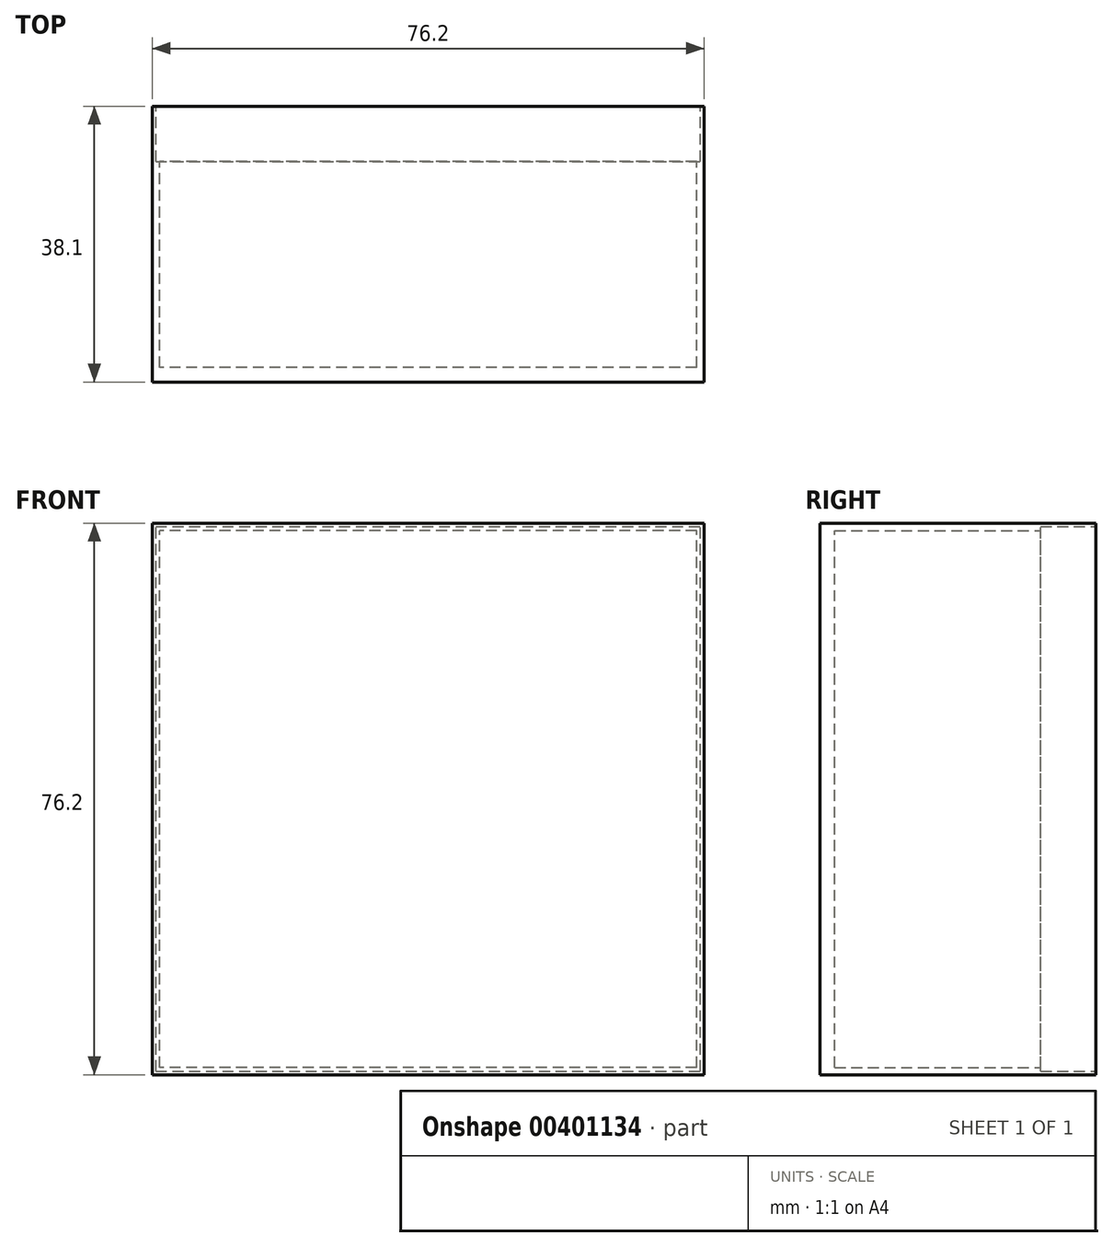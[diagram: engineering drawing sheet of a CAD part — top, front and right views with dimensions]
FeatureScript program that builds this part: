
annotation { "Feature Type Name" : "Feature", "Feature Type Description" : "" }
export const myFeature = defineFeature(function(context is Context, id is Id, definition is map)
    precondition{}
    {
        {
            var Q0;
            Q0=qCreatedBy(makeId("Front.planeOp"),FACE);
            var sketch = newSketch(context, id + "F0", { "sketchPlane" : qUnion([Q0])});
            skLineSegment(sketch, "E0.bottom", {"start": v(38.1, -38.1) * mm, "end": v(-38.1, -38.1) * mm});
            skLineSegment(sketch, "E0.top", {"start": v(38.1, 38.1) * mm, "end": v(-38.1, 38.1) * mm});
            skLineSegment(sketch, "E0.left", {"start": v(38.1, -38.1) * mm, "end": v(38.1, 38.1) * mm});
            skLineSegment(sketch, "E0.right", {"start": v(-38.1, -38.1) * mm, "end": v(-38.1, 38.1) * mm});
            skPoint(sketch, "E0.middle", {"position": v(0, 0) * mm});
            skSolve(sketch);
        }
        {
            var Q0;
            Q0=makeQuery(id+"F0.imprint","IMPRINT",FACE,{"disambiguationData":[TD([[makeQuery(id+"F0.imprint","IMPRINT",EDGE,{"derivedFrom":sQuery(id+"F0.wireOp",EDGE,"E0.bottom")}),-1.0]])]});
            extrude(context, id + "F1", {"entities" : qUnion([Q0]), "depth" : 38.1 * mm});
        }
        {
            var Q0;
            Q0=makeQuery(id+"F1.opExtrude","CAP_FACE",FACE,{"disambiguationData":[OSD([sQuery(id+"F0.wireOp",EDGE,"E0.bottom"),sQuery(id+"F0.wireOp",EDGE,"E0.top"),sQuery(id+"F0.wireOp",EDGE,"E0.left"),sQuery(id+"F0.wireOp",EDGE,"E0.right")])],"isStart":true});
            var sketch = newSketch(context, id + "F2", { "sketchPlane" : qUnion([Q0])});
            skLineSegment(sketch, "E1.bottom", {"start": v(-37.08, -37.08) * mm, "end": v(37.08, -37.08) * mm});
            skLineSegment(sketch, "E1.top", {"start": v(-37.08, 37.08) * mm, "end": v(37.08, 37.08) * mm});
            skLineSegment(sketch, "E1.left", {"start": v(-37.08, -37.08) * mm, "end": v(-37.08, 37.08) * mm});
            skLineSegment(sketch, "E1.right", {"start": v(37.08, -37.08) * mm, "end": v(37.08, 37.08) * mm});
            skPoint(sketch, "E1.middle", {"position": v(0, 0) * mm});
            skSolve(sketch);
        }
        {
            var Q0;
            Q0=makeQuery(id+"F2.imprint","IMPRINT",FACE,{"disambiguationData":[TD([[makeQuery(id+"F2.imprint","IMPRINT",EDGE,{"derivedFrom":sQuery(id+"F2.wireOp",EDGE,"E1.bottom")}),1.0]])]});
            extrude(context, id + "F3", {"entities" : qUnion([Q0]), "operationType" : NewBodyOperationType.REMOVE, "oppositeDirection" : true, "depth" : 36.07 * mm});
        }
        {
            var Q0;
            Q0=makeQuery(id+"F1.opExtrude","CAP_FACE",FACE,{"disambiguationData":[OSD([sQuery(id+"F0.wireOp",EDGE,"E0.bottom"),sQuery(id+"F0.wireOp",EDGE,"E0.top"),sQuery(id+"F0.wireOp",EDGE,"E0.left"),sQuery(id+"F0.wireOp",EDGE,"E0.right")])],"isStart":true});
            var sketch = newSketch(context, id + "F4", { "sketchPlane" : qUnion([Q0])});
            skLineSegment(sketch, "E2.bottom", {"start": v(37.6, -37.6) * mm, "end": v(-37.6, -37.6) * mm});
            skLineSegment(sketch, "E2.top", {"start": v(37.6, 37.6) * mm, "end": v(-37.6, 37.6) * mm});
            skLineSegment(sketch, "E2.left", {"start": v(37.6, -37.6) * mm, "end": v(37.6, 37.6) * mm});
            skLineSegment(sketch, "E2.right", {"start": v(-37.6, -37.6) * mm, "end": v(-37.6, 37.6) * mm});
            skPoint(sketch, "E2.middle", {"position": v(0, 0) * mm});
            skLineSegment(sketch, "E3.bottom", {"start": v(37.08, -37.08) * mm, "end": v(-37.08, -37.08) * mm});
            skLineSegment(sketch, "E3.top", {"start": v(37.08, 37.08) * mm, "end": v(-37.08, 37.08) * mm});
            skLineSegment(sketch, "E3.left", {"start": v(37.08, -37.08) * mm, "end": v(37.08, 37.08) * mm});
            skLineSegment(sketch, "E3.right", {"start": v(-37.08, -37.08) * mm, "end": v(-37.08, 37.08) * mm});
            skSolve(sketch);
        }
        {
            var Q0;
            Q0=makeQuery(id+"F4.imprint","IMPRINT",FACE,{"disambiguationData":[TD([[makeQuery(id+"F4.imprint","IMPRINT",EDGE,{"derivedFrom":sQuery(id+"F4.wireOp",EDGE,"E2.bottom")}),-1.0]])]});
            extrude(context, id + "F5", {"entities" : qUnion([Q0]), "operationType" : NewBodyOperationType.REMOVE, "oppositeDirection" : true, "depth" : 7.62 * mm});
        }
    });
